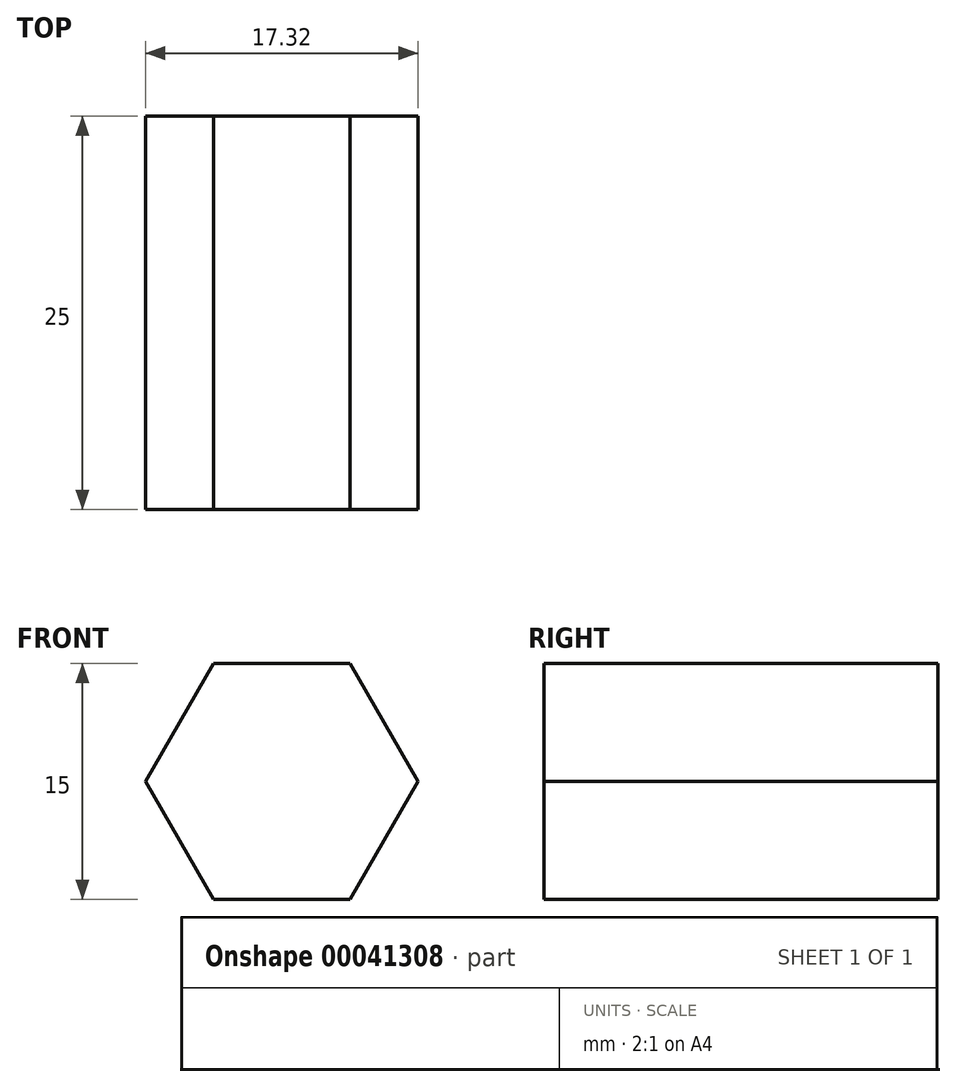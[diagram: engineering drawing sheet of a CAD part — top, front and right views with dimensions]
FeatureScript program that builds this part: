
annotation { "Feature Type Name" : "Feature", "Feature Type Description" : "" }
export const myFeature = defineFeature(function(context is Context, id is Id, definition is map)
    precondition{}
    {
        {
            var Q0;
            Q0=qCreatedBy(makeId("Front.planeOp"),FACE);
            var sketch = newSketch(context, id + "F0", { "sketchPlane" : qUnion([Q0])});
            skCircle(sketch, "E0.cCircle", {"center": v(0, 0) * mm, "radius": 7.5 * mm, "construction": true});
            skLineSegment(sketch, "E0.0", {"start": v(4.33, 7.5) * mm, "end": v(8.66, 0) * mm});
            skLineSegment(sketch, "E0.1", {"start": v(8.66, 0) * mm, "end": v(4.33, -7.5) * mm});
            skLineSegment(sketch, "E0.2", {"start": v(4.33, -7.5) * mm, "end": v(-4.33, -7.5) * mm});
            skLineSegment(sketch, "E0.3", {"start": v(-4.33, -7.5) * mm, "end": v(-8.66, 0) * mm});
            skLineSegment(sketch, "E0.4", {"start": v(-8.66, 0) * mm, "end": v(-4.33, 7.5) * mm});
            skLineSegment(sketch, "E0.5", {"start": v(-4.33, 7.5) * mm, "end": v(4.33, 7.5) * mm});
            skPoint(sketch, "E0.0.midPoint", {"position": v(6.5, 3.75) * mm});
            skSolve(sketch);
        }
        {
            var Q0;
            Q0=makeQuery(id+"F0.imprint","IMPRINT",FACE,{"disambiguationData":[TD([[makeQuery(id+"F0.imprint","IMPRINT",EDGE,{"derivedFrom":sQuery(id+"F0.wireOp",EDGE,"E0.0")}),-1.0]])]});
            extrude(context, id + "F1", {"entities" : qUnion([Q0]), "depth" : 25 * mm});
        }
    });
